# Revit family: Hager-Vega-IP40-sistema-NoHosted-ES-es
name_source: partatom
category: Electrical Equipment
units: mm (PartAtom-declared; Revit-internal decimal feet)

## family parameters
Always vertical = Yes
Cut with Voids When Loaded = No
Panel Configuration = Two Columns, Circuits Across
Part Type = Panelboard
Room Calculation Point = No
Round Connector Dimension = Use Diameter
Shared = No
Work Plane-Based = Yes

## types (8) — shared parameters
Default Elevation = 1219 mm
EF000003 - Tipo de montaje = EV000384 - Montado superficial (escayola)
EF000007 - Color = EV000202 - Blanco
EF000008 - Anchura = 400 mm  [stored 1.31234 ft]
EF000049 - Profundidad = 146 mm  [stored 0.479003 ft]
EF000116 - Número RAL = 9010
EF000118 - Con placa de montaje = No
EF000339 - Tipo de cubierta = EV004216 - Puerta
EF001062 - Versión de EMC = No
EF001088 - Posibilidad de extensión = Yes
EF001131 - Profundidad interna = 120 mm
EF001134 - Carril DIN = Yes
EF001596 - Material de la carcasa = EV000139 - Plástico
EF002950 - Anchura de unidades de división = 18
EF004462 - Tipo de cierre = EV000154 - Otros
EF005474 - Grado de protección (IP) = EV006415 - IP40
EF006306 - Con cierre = No
EF009212 - Versión de la cubierta = EV000116 - Cerrado
EF015776 - Borne de tierra = Yes
EF015777 - Borne neutro = No
EF015941 - Puerta de transmisión de señal = Yes
HG000001 - Número de columnas = 1
HG000002 - Con puerta o tapa = Yes
HG000003 - Gama = Vega
HG000005 - Grosor = 3 mm  [stored 0.00984252 ft]
HG000006 - Empotrado = No
HG000009 - Puerta batiente doble = No
HG000010 - Puertas asimétricas = No
HG000011 - Filas vacías desde abajo = No
HG000017 - Distancia entre polos = 18 mm  [stored 0.0590551 ft]
Manufacturer = Hager
Type Comments = Vega
zero-valued in all types: EF000218 - Profundidad de instalación, EF000332 - Altura de la instalación, EF000846 - Anchura de instalación, HG000007 - Número de columnas vacías, HG000008 - Número de filas vacías

## per-type parameters (varying)
| type | EF000040 - Altura | EF000266 - Número de filas | EF006244 - Tapa/puerta transparente | HG000004 - Referencia del fabricante | Model |
| Montado superficial IP40 A400 A325 P146 18 unidad de división - VB118PE | 325 mm | 1 | No | VB118PE | VB118PE |
| Montado superficial IP40 A400 A325 P146 18 unidad de división - VB118TE | 325 mm | 1 | Yes | VB118TE | VB118TE |
| Montado superficial IP40 A400 A475 P146 18 unidad de división - VB218PE | 475 mm  [stored 1.5584 ft] | 2 | No | VB218PE | VB218PE |
| Montado superficial IP40 A400 A475 P146 18 unidad de división - VB218TE | 475 mm  [stored 1.5584 ft] | 2 | Yes | VB218TE | VB218TE |
| Montado superficial IP40 A400 A625 P146 18 unidad de división - VB318PE | 625 mm  [stored 2.05052 ft] | 3 | No | VB318PE | VB318PE |
| Montado superficial IP40 A400 A625 P146 18 unidad de división - VB318TE | 625 mm  [stored 2.05052 ft] | 3 | Yes | VB318TE | VB318TE |
| Montado superficial IP40 A400 A775 P146 18 unidad de división - VB418PE | 775 mm  [stored 2.54265 ft] | 4 | No | VB418PE | VB418PE |
| Montado superficial IP40 A400 A775 P146 18 unidad de división - VB418TE | 775 mm  [stored 2.54265 ft] | 4 | Yes | VB418TE | VB418TE |

note: [stored X ft] marks values corroborated as IEEE doubles in the binary element streams (Revit-internal decimal feet)

## geometry (parser evidence)
native form markers: Sweep x13
no freeform markers — native parametric forms only
